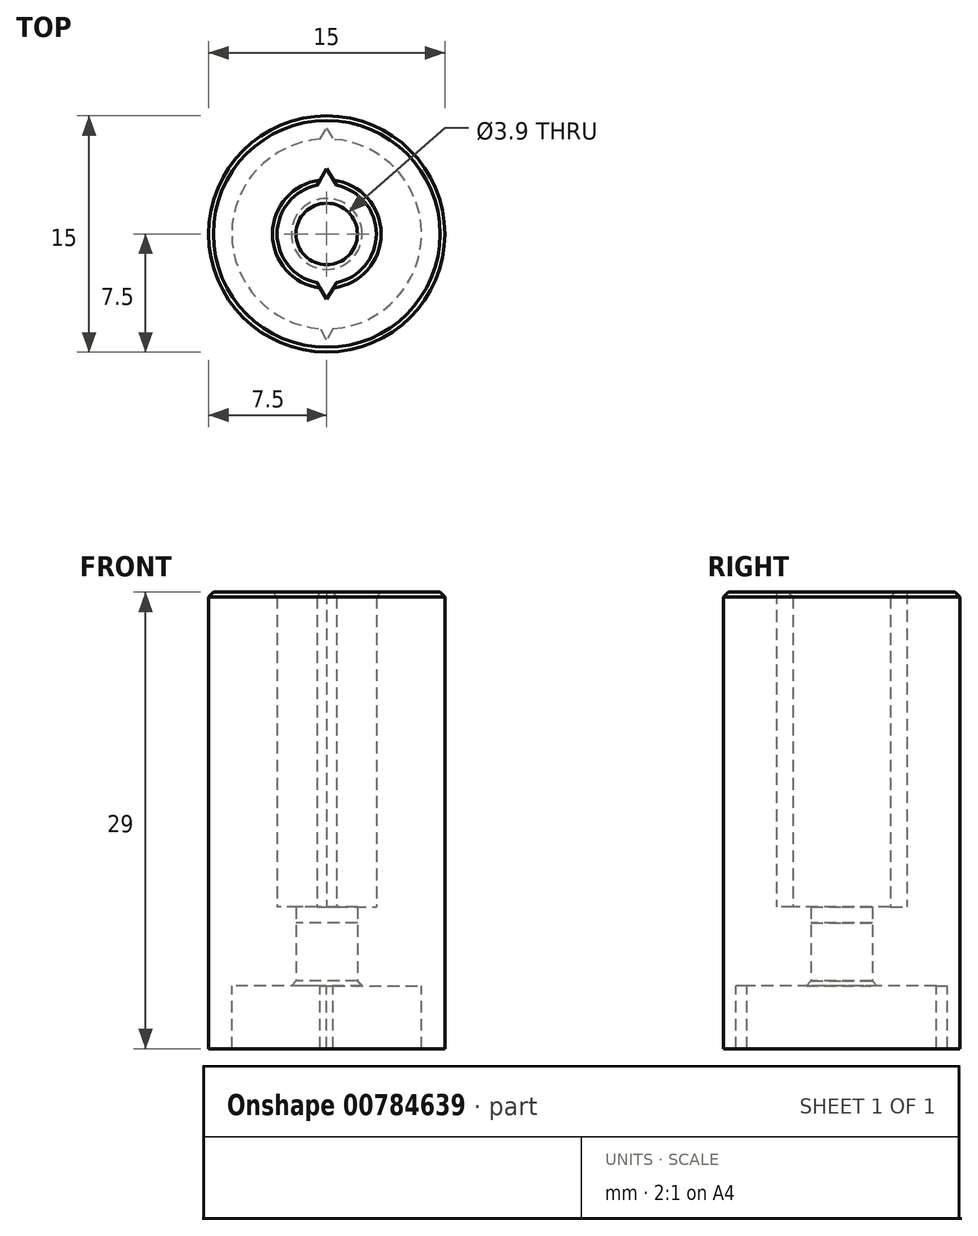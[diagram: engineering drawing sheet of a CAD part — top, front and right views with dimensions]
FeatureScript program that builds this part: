
annotation { "Feature Type Name" : "Feature", "Feature Type Description" : "" }
export const myFeature = defineFeature(function(context is Context, id is Id, definition is map)
    precondition{}
    {
        {
            var Q0;
            Q0=qCreatedBy(makeId("Top.planeOp"),FACE);
            var sketch = newSketch(context, id + "F0", { "sketchPlane" : qUnion([Q0])});
            skCircle(sketch, "E0", {"center": v(0, 0) * mm, "radius": 3.15 * mm});
            skCircle(sketch, "E1", {"center": v(0, 0) * mm, "radius": 4.5 * mm});
            skCircle(sketch, "E2", {"center": v(0, 0) * mm, "radius": 1.95 * mm});
            skCircle(sketch, "E3", {"center": v(0, 0) * mm, "radius": 6.03 * mm});
            skCircle(sketch, "E4", {"center": v(0, 0) * mm, "radius": 7.5 * mm});
            skCircle(sketch, "E5.cCircle", {"center": v(0, 3.15) * mm, "radius": 0.5 * mm, "construction": true});
            skLineSegment(sketch, "E5.0", {"start": v(0.87, 2.65) * mm, "end": v(-0.87, 2.65) * mm});
            skLineSegment(sketch, "E5.1", {"start": v(-0.87, 2.65) * mm, "end": v(0, 4.15) * mm});
            skLineSegment(sketch, "E5.2", {"start": v(0, 4.15) * mm, "end": v(0.87, 2.65) * mm});
            skPoint(sketch, "E5.0.midPoint", {"position": v(0, 2.65) * mm});
            skCircle(sketch, "E6.cCircle", {"center": v(0, 6.03) * mm, "radius": 0.35 * mm, "construction": true});
            skLineSegment(sketch, "E6.0", {"start": v(0.6, 5.68) * mm, "end": v(-0.6, 5.68) * mm});
            skLineSegment(sketch, "E6.1", {"start": v(-0.6, 5.68) * mm, "end": v(0, 6.73) * mm});
            skLineSegment(sketch, "E6.2", {"start": v(0, 6.73) * mm, "end": v(0.6, 5.68) * mm});
            skPoint(sketch, "E6.0.midPoint", {"position": v(0, 5.68) * mm});
            skCircle(sketch, "E7.cCircle", {"center": v(0, -3.15) * mm, "radius": 0.5 * mm, "construction": true});
            skLineSegment(sketch, "E7.0", {"start": v(-0.87, -2.65) * mm, "end": v(0.87, -2.65) * mm});
            skLineSegment(sketch, "E7.1", {"start": v(0.87, -2.65) * mm, "end": v(0, -4.15) * mm});
            skLineSegment(sketch, "E7.2", {"start": v(0, -4.15) * mm, "end": v(-0.87, -2.65) * mm});
            skPoint(sketch, "E7.0.midPoint", {"position": v(0, -2.65) * mm});
            skCircle(sketch, "E8.cCircle", {"center": v(0, -6.03) * mm, "radius": 0.35 * mm, "construction": true});
            skLineSegment(sketch, "E8.0", {"start": v(-0.6, -5.68) * mm, "end": v(0.6, -5.68) * mm});
            skLineSegment(sketch, "E8.1", {"start": v(0.6, -5.68) * mm, "end": v(0, -6.73) * mm});
            skLineSegment(sketch, "E8.2", {"start": v(0, -6.73) * mm, "end": v(-0.6, -5.68) * mm});
            skPoint(sketch, "E8.0.midPoint", {"position": v(0, -5.68) * mm});
            skSolve(sketch);
        }
        {
            var Q0;
            Q0=makeQuery(id+"F0.imprint","IMPRINT",FACE,{"disambiguationData":[TD([[makeQuery(id+"F0.imprint","IMPRINT",EDGE,{"derivedFrom":sQuery(id+"F0.wireOp",EDGE,"E1")}),-1.0]])]});
            var Q1;
            Q1=makeQuery(id+"F0.imprint","IMPRINT",FACE,{"disambiguationData":[TD([[makeQuery(id+"F0.imprint","IMPRINT",EDGE,{"derivedFrom":sQuery(id+"F0.wireOp",EDGE,"E3")}),-1.0]])]});
            var Q2;
            Q2=makeQuery(id+"F0.imprint","IMPRINT",FACE,{"disambiguationData":[TD([[makeQuery(id+"F0.imprint","IMPRINT",EDGE,{"derivedFrom":sQuery(id+"F0.wireOp",EDGE,"E1")}),1.0]])]});
            var Q3;
            Q3=makeQuery(id+"F0.imprint","IMPRINT",FACE,{"disambiguationData":[TD([[makeQuery(id+"F0.imprint","IMPRINT",EDGE,{"derivedFrom":sQuery(id+"F0.wireOp",EDGE,"E4")}),1.0]])]});
            var Q4;
            {var subQ5=sQuery(id+"F0.wireOp",EDGE,"E8.0");Q4=makeQuery(id+"F0.imprint","IMPRINT",FACE,{"disambiguationData":[TD([[makeQuery(id+"F0.imprint","IMPRINT",EDGE,{"derivedFrom":subQ5}),-1.0]])]});}
            var Q5;
            {var subQ0=sQuery(id+"F0.wireOp",EDGE,"E8.2");var subQ1=sQuery(id+"F0.wireOp",EDGE,"E3");var subQ2=makeQuery(id+"F0.imprint","INTERSECT",VERTEX,{"derivedFrom":[subQ1,subQ0]});Q5=makeQuery(id+"F0.imprint","IMPRINT",FACE,{"disambiguationData":[TD([[makeQuery(id+"F0.imprint","IMPRINT",EDGE,{"disambiguationData":[TD([[subQ2,-1.0]])],"derivedFrom":subQ1}),-1.0]])]});}
            var Q6;
            {var subQ0=sQuery(id+"F0.wireOp",EDGE,"E6.1");var subQ1=sQuery(id+"F0.wireOp",EDGE,"E3");var subQ2=makeQuery(id+"F0.imprint","INTERSECT",VERTEX,{"derivedFrom":[subQ1,subQ0]});Q6=makeQuery(id+"F0.imprint","IMPRINT",FACE,{"disambiguationData":[TD([[makeQuery(id+"F0.imprint","IMPRINT",EDGE,{"disambiguationData":[TD([[subQ2,1.0]])],"derivedFrom":subQ1}),-1.0]])]});}
            var Q7;
            {var subQ5=sQuery(id+"F0.wireOp",EDGE,"E6.0");Q7=makeQuery(id+"F0.imprint","IMPRINT",FACE,{"disambiguationData":[TD([[makeQuery(id+"F0.imprint","IMPRINT",EDGE,{"derivedFrom":subQ5}),-1.0]])]});}
            extrude(context, id + "F1", {"entities" : qUnion([Q0, Q1, Q2, Q3, Q4, Q5, Q6, Q7]), "depth" : 25 * mm, "offsetDistance" : 25 * mm});
        }
        {
            var Q0;
            Q0=makeQuery(id+"F0.imprint","IMPRINT",FACE,{"disambiguationData":[TD([[makeQuery(id+"F0.imprint","IMPRINT",EDGE,{"derivedFrom":sQuery(id+"F0.wireOp",EDGE,"E0")}),1.0]])]});
            var Q1;
            Q1=makeQuery(id+"F0.imprint","IMPRINT",FACE,{"disambiguationData":[TD([[makeQuery(id+"F0.imprint","IMPRINT",EDGE,{"derivedFrom":sQuery(id+"F0.wireOp",EDGE,"E1")}),-1.0]])]});
            var Q2;
            Q2=makeQuery(id+"F0.imprint","IMPRINT",FACE,{"disambiguationData":[TD([[makeQuery(id+"F0.imprint","IMPRINT",EDGE,{"derivedFrom":sQuery(id+"F0.wireOp",EDGE,"E3")}),-1.0]])]});
            var Q3;
            Q3=makeQuery(id+"F0.imprint","IMPRINT",FACE,{"disambiguationData":[TD([[makeQuery(id+"F0.imprint","IMPRINT",EDGE,{"derivedFrom":sQuery(id+"F0.wireOp",EDGE,"E2")}),-1.0]])]});
            var Q4;
            Q4=makeQuery(id+"F0.imprint","IMPRINT",FACE,{"disambiguationData":[TD([[makeQuery(id+"F0.imprint","IMPRINT",EDGE,{"derivedFrom":sQuery(id+"F0.wireOp",EDGE,"E4")}),1.0]])]});
            var Q5;
            Q5=makeQuery(id+"F1.opExtrude","CAP_FACE",FACE,{"disambiguationData":[OSD([sQuery(id+"F0.wireOp",EDGE,"E3"),sQuery(id+"F0.wireOp",EDGE,"E6.1"),sQuery(id+"F0.wireOp",EDGE,"E6.2")])],"isStart":false});
            var Q6;
            Q6=makeQuery(id+"F0.imprint","IMPRINT",FACE,{"disambiguationData":[TD([[makeQuery(id+"F0.imprint","IMPRINT",EDGE,{"derivedFrom":sQuery(id+"F0.wireOp",EDGE,"E1")}),1.0]])]});
            var Q7;
            {var subQ0=sQuery(id+"F0.wireOp",EDGE,"E7.2");var subQ1=sQuery(id+"F0.wireOp",EDGE,"E0");var subQ2=makeQuery(id+"F0.imprint","INTERSECT",VERTEX,{"derivedFrom":[subQ1,subQ0]});Q7=makeQuery(id+"F0.imprint","IMPRINT",FACE,{"disambiguationData":[TD([[makeQuery(id+"F0.imprint","IMPRINT",EDGE,{"disambiguationData":[TD([[subQ2,-1.0]])],"derivedFrom":subQ1}),-1.0]])]});}
            var Q8;
            {var subQ5=sQuery(id+"F0.wireOp",EDGE,"E7.0");Q8=makeQuery(id+"F0.imprint","IMPRINT",FACE,{"disambiguationData":[TD([[makeQuery(id+"F0.imprint","IMPRINT",EDGE,{"derivedFrom":subQ5}),-1.0]])]});}
            var Q9;
            {var subQ5=sQuery(id+"F0.wireOp",EDGE,"E5.0");Q9=makeQuery(id+"F0.imprint","IMPRINT",FACE,{"disambiguationData":[TD([[makeQuery(id+"F0.imprint","IMPRINT",EDGE,{"derivedFrom":subQ5}),-1.0]])]});}
            var Q10;
            {var subQ0=sQuery(id+"F0.wireOp",EDGE,"E5.1");var subQ1=sQuery(id+"F0.wireOp",EDGE,"E0");var subQ2=makeQuery(id+"F0.imprint","INTERSECT",VERTEX,{"derivedFrom":[subQ1,subQ0]});Q10=makeQuery(id+"F0.imprint","IMPRINT",FACE,{"disambiguationData":[TD([[makeQuery(id+"F0.imprint","IMPRINT",EDGE,{"disambiguationData":[TD([[subQ2,1.0]])],"derivedFrom":subQ1}),-1.0]])]});}
            var Q11;
            {var subQ0=sQuery(id+"F0.wireOp",EDGE,"E6.1");var subQ1=sQuery(id+"F0.wireOp",EDGE,"E3");var subQ2=makeQuery(id+"F0.imprint","INTERSECT",VERTEX,{"derivedFrom":[subQ1,subQ0]});Q11=makeQuery(id+"F0.imprint","IMPRINT",FACE,{"disambiguationData":[TD([[makeQuery(id+"F0.imprint","IMPRINT",EDGE,{"disambiguationData":[TD([[subQ2,1.0]])],"derivedFrom":subQ1}),-1.0]])]});}
            var Q12;
            {var subQ5=sQuery(id+"F0.wireOp",EDGE,"E8.0");Q12=makeQuery(id+"F0.imprint","IMPRINT",FACE,{"disambiguationData":[TD([[makeQuery(id+"F0.imprint","IMPRINT",EDGE,{"derivedFrom":subQ5}),-1.0]])]});}
            var Q13;
            {var subQ0=sQuery(id+"F0.wireOp",EDGE,"E8.2");var subQ1=sQuery(id+"F0.wireOp",EDGE,"E3");var subQ2=makeQuery(id+"F0.imprint","INTERSECT",VERTEX,{"derivedFrom":[subQ1,subQ0]});Q13=makeQuery(id+"F0.imprint","IMPRINT",FACE,{"disambiguationData":[TD([[makeQuery(id+"F0.imprint","IMPRINT",EDGE,{"disambiguationData":[TD([[subQ2,-1.0]])],"derivedFrom":subQ1}),-1.0]])]});}
            var Q14;
            {var subQ5=sQuery(id+"F0.wireOp",EDGE,"E6.0");Q14=makeQuery(id+"F0.imprint","IMPRINT",FACE,{"disambiguationData":[TD([[makeQuery(id+"F0.imprint","IMPRINT",EDGE,{"derivedFrom":subQ5}),-1.0]])]});}
            extrude(context, id + "F2", {"entities" : qUnion([Q0, Q1, Q2, Q3, Q4, Q5, Q6, Q7, Q8, Q9, Q10, Q11, Q12, Q13, Q14]), "operationType" : NewBodyOperationType.ADD, "depth" : 5 * mm, "offsetDistance" : 25 * mm});
        }
        {
            var Q0;
            Q0=makeQuery(id+"F0.imprint","IMPRINT",FACE,{"disambiguationData":[TD([[makeQuery(id+"F0.imprint","IMPRINT",EDGE,{"derivedFrom":sQuery(id+"F0.wireOp",EDGE,"E4")}),1.0]])]});
            extrude(context, id + "F3", {"entities" : qUnion([Q0]), "operationType" : NewBodyOperationType.ADD, "oppositeDirection" : true, "depth" : 4 * mm, "offsetDistance" : 25 * mm});
        }
        {
            var Q0;
            Q0=makeQuery(id+"F1.opExtrude","CAP_EDGE",EDGE,{"disambiguationData":[OSD([sQuery(id+"F0.wireOp",EDGE,"E4")])],"isStart":false});
            var Q1;
            Q1=makeQuery(id+"F1.opExtrude","CAP_EDGE",EDGE,{"disambiguationData":[OSD([sQuery(id+"F0.wireOp",EDGE,"E0")])],"isStart":false});
            var Q2;
            Q2=makeQuery(id+"F2.opExtrude","CAP_EDGE",EDGE,{"disambiguationData":[OSD([sQuery(id+"F0.wireOp",EDGE,"E2")])],"isStart":true});
            chamfer(context, id + "F4", {"entities" : qUnion([Q0, Q1, Q2]), "width" : 0.3 * mm, "tangentPropagation" : true});
        }
        {
            var Q0;
            Q0=makeQuery(id+"F0.imprint","IMPRINT",FACE,{"disambiguationData":[TD([[makeQuery(id+"F0.imprint","IMPRINT",EDGE,{"derivedFrom":sQuery(id+"F0.wireOp",EDGE,"E2")}),1.0]])]});
            var Q1;
            Q1=makeQuery(id+"F2.opExtrude","CAP_FACE",FACE,{"disambiguationData":[OSD([sQuery(id+"F0.wireOp",EDGE,"E0"),sQuery(id+"F0.wireOp",EDGE,"E2"),sQuery(id+"F0.wireOp",EDGE,"E5.1"),sQuery(id+"F0.wireOp",EDGE,"E5.2")])],"isStart":false});
            var Q2;
            Q2=makeQuery(id+"F2.opExtrude","CAP_FACE",FACE,{"disambiguationData":[OSD([sQuery(id+"F0.wireOp",EDGE,"E0"),sQuery(id+"F0.wireOp",EDGE,"E2"),sQuery(id+"F0.wireOp",EDGE,"E5.1"),sQuery(id+"F0.wireOp",EDGE,"E5.2")])],"isStart":false});
            extrude(context, id + "F5", {"entities" : qUnion([Q0]), "endBound" : BoundingType.UP_TO_SURFACE, "depth" : 25 * mm, "endBoundEntityFace" : qUnion([Q1]), "offsetDistance" : 25 * mm, "hasSecondDirection" : true, "secondDirectionBound" : BoundingType.UP_TO_SURFACE, "secondDirectionOppositeDirection" : false, "secondDirectionDepth" : 25 * mm, "secondDirectionBoundEntityFace" : qUnion([Q2]), "hasSecondDirectionOffset" : true, "secondDirectionOffsetDistance" : 1 * mm});
        }
    });
